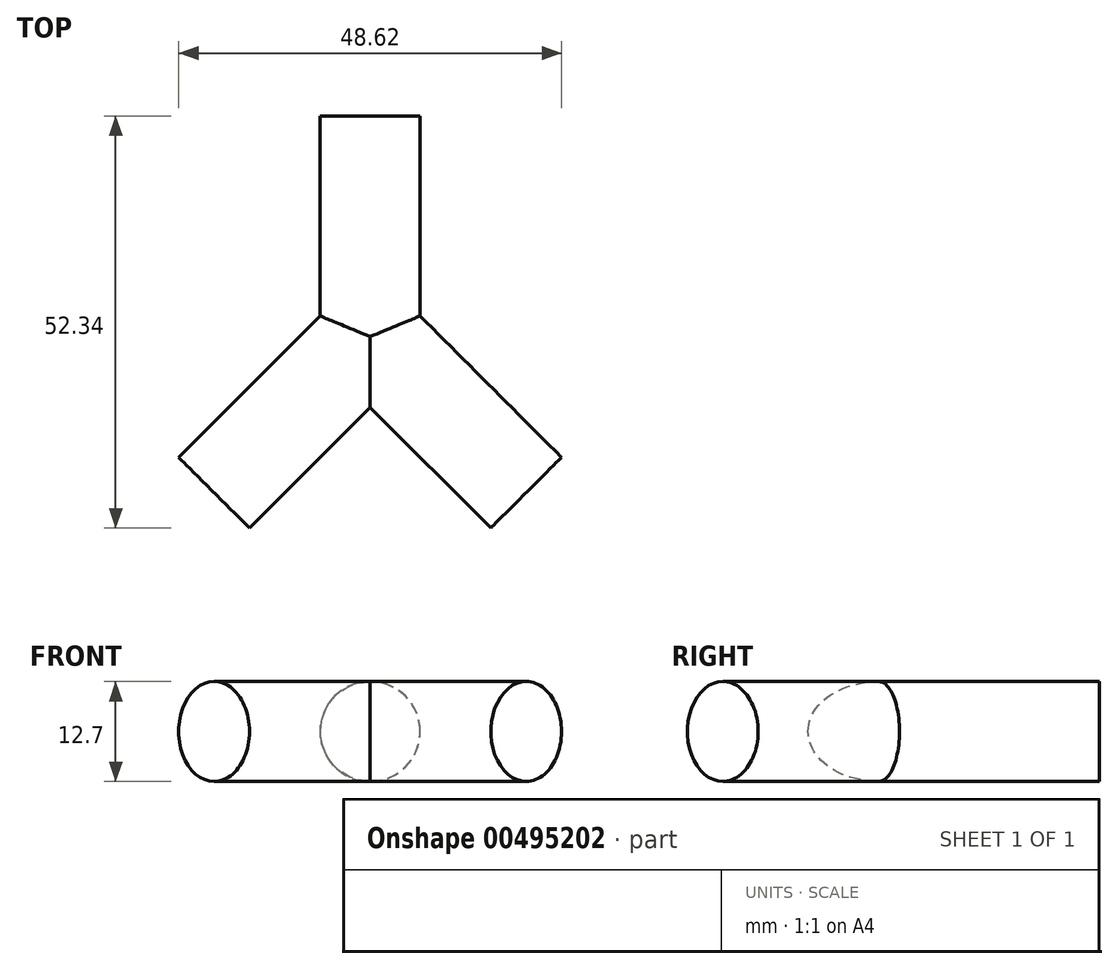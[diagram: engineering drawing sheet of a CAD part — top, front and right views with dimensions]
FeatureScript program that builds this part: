
annotation { "Feature Type Name" : "Feature", "Feature Type Description" : "" }
export const myFeature = defineFeature(function(context is Context, id is Id, definition is map)
    precondition{}
    {
        {
            var Q0;
            Q0=qCreatedBy(makeId("Top.planeOp"),FACE);
            var sketch = newSketch(context, id + "F0", { "sketchPlane" : qUnion([Q0])});
            skLineSegment(sketch, "E0.bottom", {"start": v(-6.35, 0) * mm, "end": v(6.35, 0) * mm});
            skLineSegment(sketch, "E0.top", {"start": v(-6.35, 25.4) * mm, "end": v(6.35, 25.4) * mm});
            skLineSegment(sketch, "E0.left", {"start": v(-6.35, 0) * mm, "end": v(-6.35, 25.4) * mm});
            skLineSegment(sketch, "E0.right", {"start": v(6.35, 0) * mm, "end": v(6.35, 25.4) * mm});
            skPoint(sketch, "E0.middle", {"position": v(0, 12.7) * mm});
            skLineSegment(sketch, "E1", {"start": v(6.35, 0) * mm, "end": v(24.31, -17.96) * mm});
            skLineSegment(sketch, "E2", {"start": v(24.31, -17.96) * mm, "end": v(15.33, -26.94) * mm});
            skLineSegment(sketch, "E3", {"start": v(15.33, -26.94) * mm, "end": v(0, -11.61) * mm});
            skLineSegment(sketch, "E4", {"start": v(0, -11.61) * mm, "end": v(-15.33, -26.94) * mm});
            skLineSegment(sketch, "E5", {"start": v(-15.33, -26.94) * mm, "end": v(-24.31, -17.96) * mm});
            skLineSegment(sketch, "E6", {"start": v(-24.31, -17.96) * mm, "end": v(-6.35, 0) * mm});
            skSolve(sketch);
        }
        {
            var Q0;
            Q0=makeQuery(id+"F0.imprint","IMPRINT",FACE,{"disambiguationData":[TD([[makeQuery(id+"F0.imprint","IMPRINT",EDGE,{"derivedFrom":sQuery(id+"F0.wireOp",EDGE,"E0.bottom")}),-1.0]])]});
            var Q1;
            Q1=makeQuery(id+"F0.imprint","IMPRINT",FACE,{"disambiguationData":[TD([[makeQuery(id+"F0.imprint","IMPRINT",EDGE,{"derivedFrom":sQuery(id+"F0.wireOp",EDGE,"E0.bottom")}),1.0]])]});
            extrude(context, id + "F1", {"entities" : qUnion([Q0, Q1]), "endBound" : BoundingType.SYMMETRIC, "depth" : 12.7 * mm});
        }
        {
            var Q0;
            Q0=makeQuery(id+"F1.opExtrude","CAP_EDGE",EDGE,{"disambiguationData":[OSD([sQuery(id+"F0.wireOp",EDGE,"E0.right")])],"isStart":false});
            var Q1;
            Q1=makeQuery(id+"F1.opExtrude","CAP_EDGE",EDGE,{"disambiguationData":[OSD([sQuery(id+"F0.wireOp",EDGE,"E0.right")])],"isStart":true});
            var Q2;
            Q2=makeQuery(id+"F1.opExtrude","CAP_EDGE",EDGE,{"disambiguationData":[OSD([sQuery(id+"F0.wireOp",EDGE,"E0.left")])],"isStart":false});
            var Q3;
            Q3=makeQuery(id+"F1.opExtrude","CAP_EDGE",EDGE,{"disambiguationData":[OSD([sQuery(id+"F0.wireOp",EDGE,"E0.left")])],"isStart":true});
            var Q4;
            Q4=makeQuery(id+"F1.opExtrude","CAP_EDGE",EDGE,{"disambiguationData":[OSD([sQuery(id+"F0.wireOp",EDGE,"E1")])],"isStart":false});
            var Q5;
            Q5=makeQuery(id+"F1.opExtrude","CAP_EDGE",EDGE,{"disambiguationData":[OSD([sQuery(id+"F0.wireOp",EDGE,"E1")])],"isStart":true});
            var Q6;
            Q6=makeQuery(id+"F1.opExtrude","CAP_EDGE",EDGE,{"disambiguationData":[OSD([sQuery(id+"F0.wireOp",EDGE,"E3")])],"isStart":false});
            var Q7;
            Q7=makeQuery(id+"F1.opExtrude","CAP_EDGE",EDGE,{"disambiguationData":[OSD([sQuery(id+"F0.wireOp",EDGE,"E3")])],"isStart":true});
            var Q8;
            Q8=makeQuery(id+"F1.opExtrude","CAP_EDGE",EDGE,{"disambiguationData":[OSD([sQuery(id+"F0.wireOp",EDGE,"E4")])],"isStart":false});
            var Q9;
            Q9=makeQuery(id+"F1.opExtrude","CAP_EDGE",EDGE,{"disambiguationData":[OSD([sQuery(id+"F0.wireOp",EDGE,"E4")])],"isStart":true});
            var Q10;
            Q10=makeQuery(id+"F1.opExtrude","CAP_EDGE",EDGE,{"disambiguationData":[OSD([sQuery(id+"F0.wireOp",EDGE,"E6")])],"isStart":false});
            var Q11;
            Q11=makeQuery(id+"F1.opExtrude","CAP_EDGE",EDGE,{"disambiguationData":[OSD([sQuery(id+"F0.wireOp",EDGE,"E6")])],"isStart":true});
            fillet(context, id + "F2", {"entities" : qUnion([Q0, Q1, Q2, Q3, Q4, Q5, Q6, Q7, Q8, Q9, Q10, Q11]), "radius" : 6.35 * mm, "tangentPropagation" : true, "allowEdgeOverflow" : false});
        }
    });
